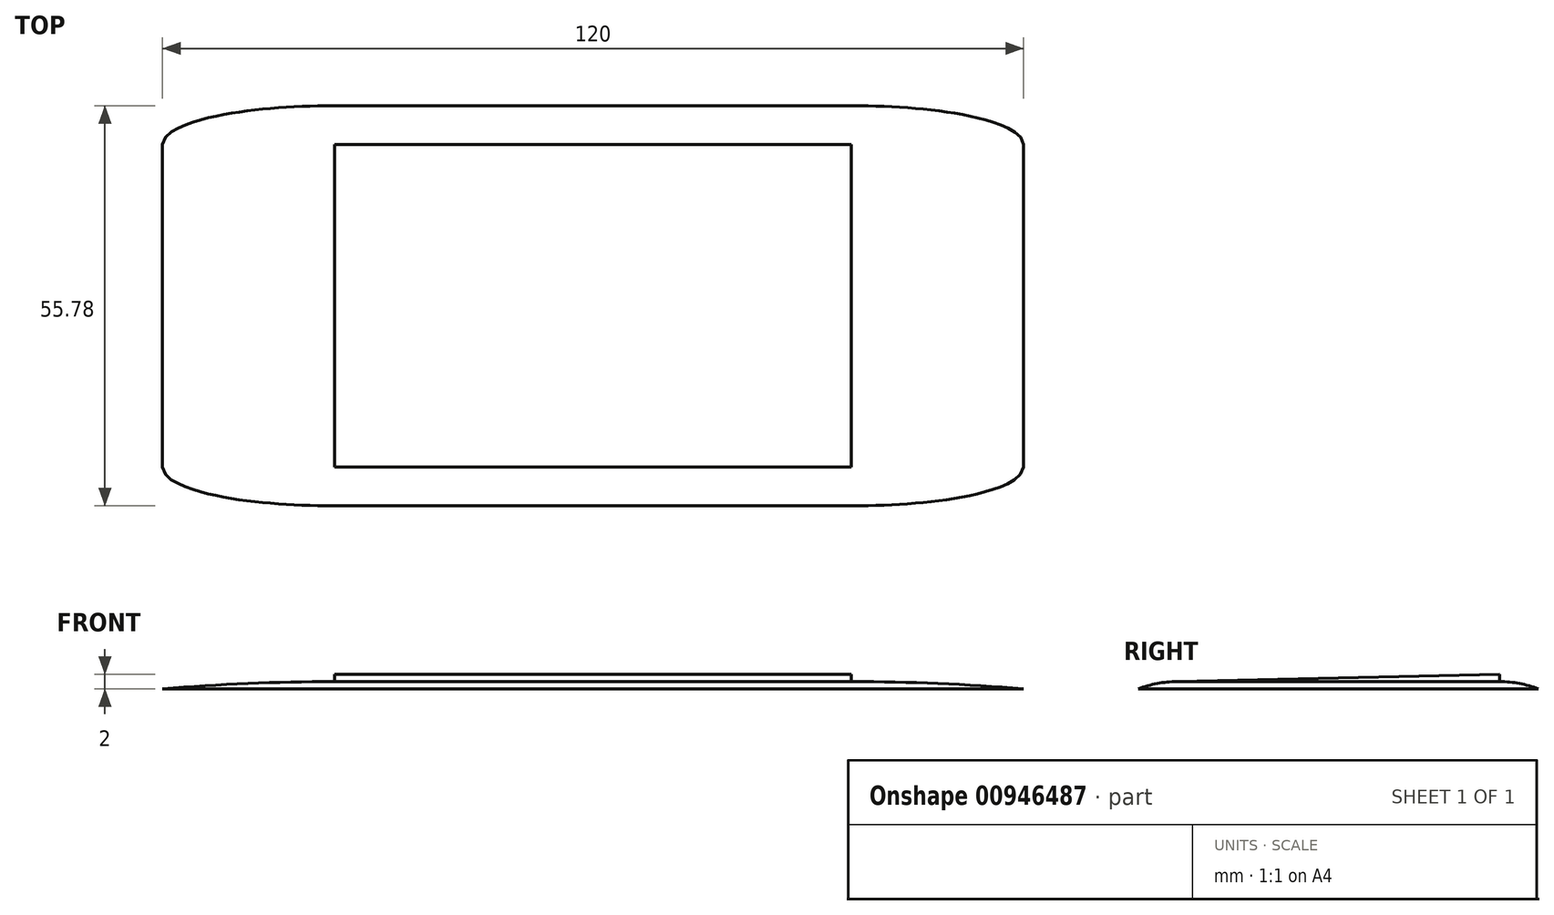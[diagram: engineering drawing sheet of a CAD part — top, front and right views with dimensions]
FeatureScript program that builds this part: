
annotation { "Feature Type Name" : "Feature", "Feature Type Description" : "" }
export const myFeature = defineFeature(function(context is Context, id is Id, definition is map)
    precondition{}
    {
        {
            var Q0;
            Q0=qCreatedBy(makeId("Top.planeOp"),FACE);
            var sketch = newSketch(context, id + "F0", { "sketchPlane" : qUnion([Q0])});
            skLineSegment(sketch, "E0.bottom", {"start": v(-60, 37.5) * mm, "end": v(60, 37.5) * mm});
            skLineSegment(sketch, "E0.top", {"start": v(-60, -37.5) * mm, "end": v(60, -37.5) * mm});
            skLineSegment(sketch, "E0.left", {"start": v(-60, 37.5) * mm, "end": v(-60, -37.5) * mm});
            skLineSegment(sketch, "E0.right", {"start": v(60, 37.5) * mm, "end": v(60, -37.5) * mm});
            skPoint(sketch, "E0.middle", {"position": v(0, 0) * mm});
            skLineSegment(sketch, "E1.bottom", {"start": v(-36, 22.5) * mm, "end": v(36, 22.5) * mm});
            skLineSegment(sketch, "E1.top", {"start": v(-36, -22.5) * mm, "end": v(36, -22.5) * mm});
            skLineSegment(sketch, "E1.left", {"start": v(-36, 22.5) * mm, "end": v(-36, -22.5) * mm});
            skLineSegment(sketch, "E1.right", {"start": v(36, 22.5) * mm, "end": v(36, -22.5) * mm});
            skLineSegment(sketch, "E2.bottom", {"start": v(-36, 22.5) * mm, "end": v(-12, 22.5) * mm});
            skLineSegment(sketch, "E2.top", {"start": v(-36, -22.5) * mm, "end": v(-12, -22.5) * mm});
            skLineSegment(sketch, "E2.right", {"start": v(-12, 22.5) * mm, "end": v(-12, -22.5) * mm});
            skLineSegment(sketch, "E3.MirrorCS", {"start": v(12, 22.5) * mm, "end": v(12, -22.5) * mm});
            skSolve(sketch);
        }
        {
            var Q0;
            Q0=makeQuery(id+"F0.imprint","IMPRINT",FACE,{"disambiguationData":[TD([[makeQuery(id+"F0.imprint","IMPRINT",EDGE,{"derivedFrom":sQuery(id+"F0.wireOp",EDGE,"E0.bottom")}),-1.0]])]});
            extrude(context, id + "F1", {"entities" : qUnion([Q0]), "depth" : 1 * mm, "offsetDistance" : 25 * mm});
        }
        {
            var Q0;
            {var subQ0=sQuery(id+"F0.wireOp",EDGE,"E1.left");Q0=makeQuery(id+"F0.imprint","IMPRINT",FACE,{"disambiguationData":[TD([[makeQuery(id+"F0.imprint","IMPRINT",EDGE,{"derivedFrom":subQ0}),1.0]])]});}
            extrude(context, id + "F2", {"entities" : qUnion([Q0]), "operationType" : NewBodyOperationType.ADD, "depth" : 2 * mm, "offsetDistance" : 25 * mm});
        }
        {
            var Q0;
            {var subQ2=sQuery(id+"F0.wireOp",EDGE,"E2.right");Q0=makeQuery(id+"F0.imprint","IMPRINT",FACE,{"disambiguationData":[TD([[makeQuery(id+"F0.imprint","IMPRINT",EDGE,{"derivedFrom":subQ2}),1.0]])]});}
            extrude(context, id + "F3", {"entities" : qUnion([Q0]), "operationType" : NewBodyOperationType.ADD, "depth" : 2 * mm, "offsetDistance" : 25 * mm});
        }
        {
            var Q0;
            {var subQ2=sQuery(id+"F0.wireOp",EDGE,"E1.right");Q0=makeQuery(id+"F0.imprint","IMPRINT",FACE,{"disambiguationData":[TD([[makeQuery(id+"F0.imprint","IMPRINT",EDGE,{"derivedFrom":subQ2}),-1.0]])]});}
            extrude(context, id + "F4", {"entities" : qUnion([Q0]), "operationType" : NewBodyOperationType.ADD, "depth" : 2 * mm, "offsetDistance" : 25 * mm});
        }
        {
            var Q0;
            Q0=makeQuery(id+"F1.opExtrude","SWEPT_FACE",FACE,{"disambiguationData":[OSD([sQuery(id+"F0.wireOp",EDGE,"E0.left")])]});
            var sketch = newSketch(context, id + "F5", { "sketchPlane" : qUnion([Q0])});
            skLineSegment(sketch, "E4.bottom", {"start": v(-22.5, 2) * mm, "end": v(22.5, 2) * mm});
            skLineSegment(sketch, "E4.top", {"start": v(-22.5, -2) * mm, "end": v(22.5, -2) * mm});
            skLineSegment(sketch, "E4.left", {"start": v(-22.5, 2) * mm, "end": v(-22.5, -2) * mm});
            skLineSegment(sketch, "E4.right", {"start": v(22.5, 2) * mm, "end": v(22.5, -2) * mm});
            skPoint(sketch, "E4.middle", {"position": v(0, 0) * mm});
            skLineSegment(sketch, "E5", {"start": v(-22.5, 2) * mm, "end": v(22.5, 1) * mm});
            skSolve(sketch);
        }
        {
            var Q0;
            {var subQ0=sQuery(id+"F5.wireOp",EDGE,"E4.bottom");Q0=makeQuery(id+"F5.imprint","IMPRINT",FACE,{"disambiguationData":[TD([[makeQuery(id+"F5.imprint","IMPRINT",EDGE,{"derivedFrom":subQ0}),-1.0]])]});}
            extrude(context, id + "F6", {"entities" : qUnion([Q0]), "operationType" : NewBodyOperationType.REMOVE, "oppositeDirection" : true, "depth" : 1000 * mm, "offsetDistance" : 25 * mm});
        }
        {
            var Q0;
            Q0=makeQuery(id+"F1.opExtrude","CAP_EDGE",EDGE,{"disambiguationData":[OSD([sQuery(id+"F0.wireOp",EDGE,"E0.left")])],"isStart":false});
            fillet(context, id + "F7", {"entities" : qUnion([Q0]), "radius" : 285 * mm, "tangentPropagation" : true, "allowEdgeOverflow" : false});
        }
        {
            var Q0;
            Q0=makeQuery(id+"F1.opExtrude","CAP_EDGE",EDGE,{"disambiguationData":[OSD([sQuery(id+"F0.wireOp",EDGE,"E0.right")])],"isStart":false});
            fillet(context, id + "F8", {"entities" : qUnion([Q0]), "radius" : 285 * mm, "tangentPropagation" : true, "allowEdgeOverflow" : false});
        }
        {
            var Q0;
            Q0=makeQuery(id+"F1.opExtrude","CAP_EDGE",EDGE,{"disambiguationData":[OSD([sQuery(id+"F0.wireOp",EDGE,"E0.top")])],"isStart":false});
            fillet(context, id + "F9", {"entities" : qUnion([Q0]), "radius" : 15 * mm, "tangentPropagation" : true, "allowEdgeOverflow" : false});
        }
        {
            var Q0;
            Q0=makeQuery(id+"F1.opExtrude","CAP_EDGE",EDGE,{"disambiguationData":[OSD([sQuery(id+"F0.wireOp",EDGE,"E0.bottom")])],"isStart":false});
            fillet(context, id + "F10", {"entities" : qUnion([Q0]), "radius" : 15 * mm, "tangentPropagation" : true, "allowEdgeOverflow" : false});
        }
    });
